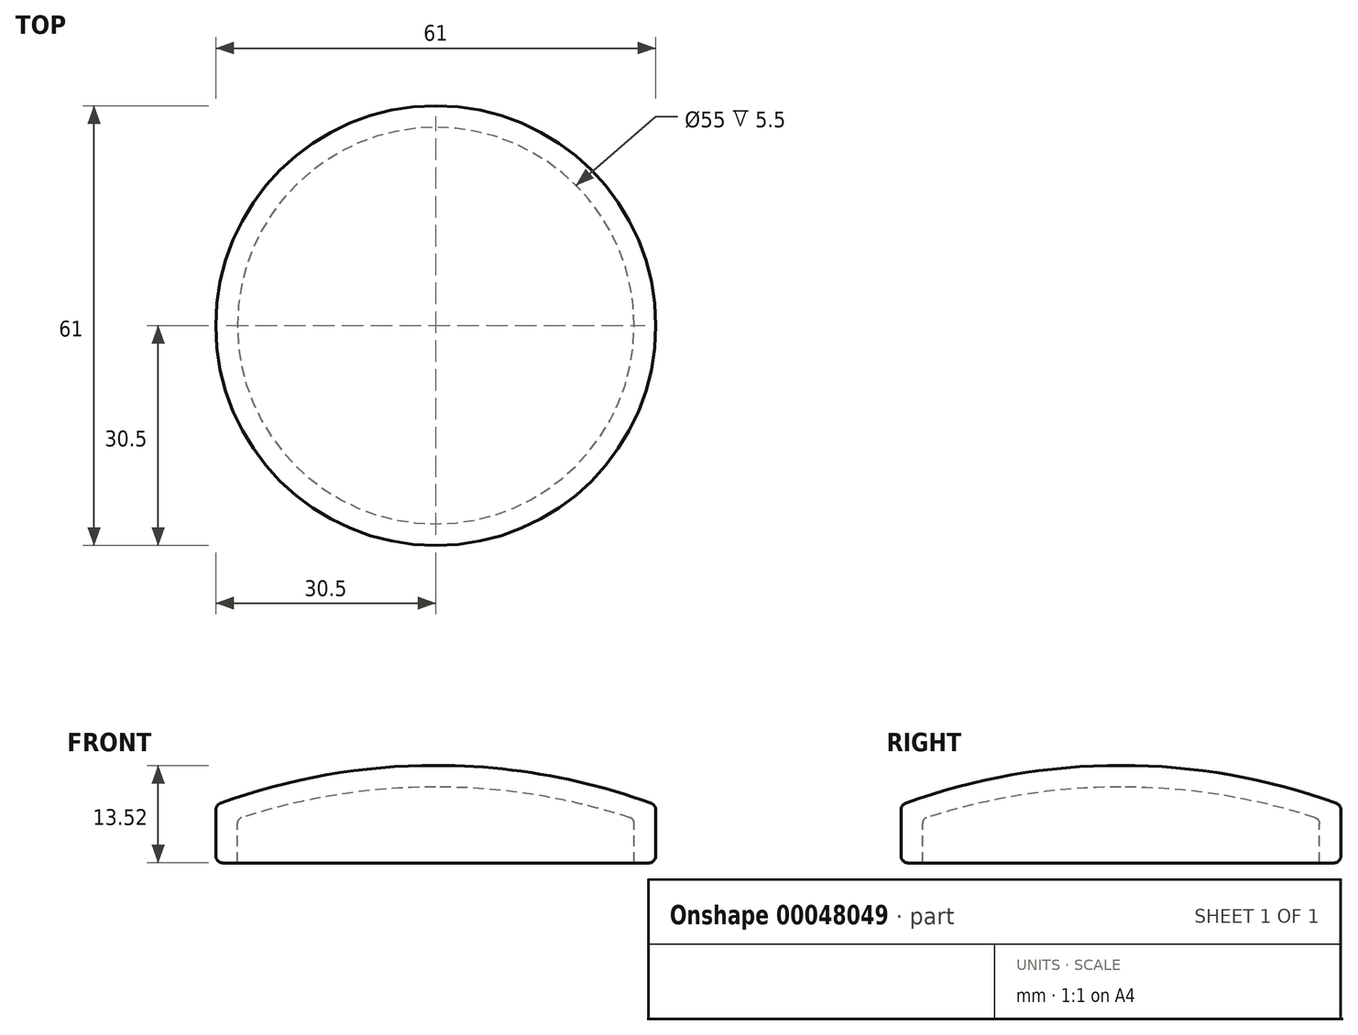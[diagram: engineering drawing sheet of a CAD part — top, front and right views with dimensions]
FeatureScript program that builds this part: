
annotation { "Feature Type Name" : "Feature", "Feature Type Description" : "" }
export const myFeature = defineFeature(function(context is Context, id is Id, definition is map)
    precondition{}
    {
        {
            var Q0;
            Q0=qCreatedBy(makeId("Front.planeOp"),FACE);
            var sketch = newSketch(context, id + "F0", { "sketchPlane" : qUnion([Q0])});
            skLineSegment(sketch, "E0", {"start": v(30.5, 8.28) * mm, "end": v(30.5, 0.26) * mm});
            skLineSegment(sketch, "E1", {"start": v(30.5, 0.26) * mm, "end": v(27.5, 0.26) * mm});
            skLineSegment(sketch, "E2", {"start": v(0, 25.47) * mm, "end": v(0, -11.75) * mm, "construction": true});
            skArc(sketch, "E3", {"start": v(30.5, 8.28) * mm, "mid": v(15.5, 12.4) * mm, "end": v(0, 13.78) * mm});
            skLineSegment(sketch, "E4", {"start": v(0, 13.78) * mm, "end": v(26.52, 13.78) * mm, "construction": true});
            skLineSegment(sketch, "E5", {"start": v(27.5, 1.6) * mm, "end": v(27.5, 1.61) * mm});
            skLineSegment(sketch, "E6", {"start": v(27.5, 0.69) * mm, "end": v(27.5, 1.6) * mm, "construction": true});
            skArc(sketch, "E7", {"start": v(26.95, 6.52) * mm, "mid": v(13.64, 9.7) * mm, "end": v(0, 10.78) * mm});
            skPoint(sketch, "E8.end.orphan", {"position": v(0, 8.36) * mm});
            skLineSegment(sketch, "E9", {"start": v(27.5, 1.61) * mm, "end": v(27.5, 5.76) * mm});
            skPoint(sketch, "E10.visualSharp", {"position": v(27.5, 6.34) * mm});
            skArc(sketch, "E10.filletArc", {"start": v(27.5, 5.76) * mm, "mid": v(27.35, 6.23) * mm, "end": v(26.95, 6.52) * mm});
            skLineSegment(sketch, "E11", {"start": v(26.95, 6.52) * mm, "end": v(26.95, 9.52) * mm, "construction": true});
            skLineSegment(sketch, "E12", {"start": v(0, 13.78) * mm, "end": v(0, 10.78) * mm});
            skLineSegment(sketch, "E13", {"start": v(27.5, 0.26) * mm, "end": v(27.5, 1.6) * mm});
            skSolve(sketch);
        }
        {
            var Q0;
            Q0=makeQuery(id+"F0.imprint","IMPRINT",FACE,{"disambiguationData":[TD([[makeQuery(id+"F0.imprint","IMPRINT",EDGE,{"derivedFrom":sQuery(id+"F0.wireOp",EDGE,"E0")}),-1.0]])]});
            var Q1;
            Q1=sQuery(id+"F0.wireOp",EDGE,"E2");
            revolve(context, id + "F1", {"entities" : qUnion([Q0]), "axis" : qUnion([Q1]), "revolveType" : RevolveType.FULL});
        }
        {
            var Q0;
            Q0=makeQuery(id+"F1.opRevolve","SWEPT_EDGE",EDGE,{"disambiguationData":[OSD([sQuery(id+"F0.wireOp",EDGE,"E0"),sQuery(id+"F0.wireOp",EDGE,"E3")])]});
            var Q1;
            Q1=makeQuery(id+"F1.opRevolve","SWEPT_EDGE",EDGE,{"disambiguationData":[OSD([sQuery(id+"F0.wireOp",EDGE,"E0"),sQuery(id+"F0.wireOp",EDGE,"E1")])]});
            fillet(context, id + "F2", {"entities" : qUnion([Q0, Q1]), "radius" : 1 * mm, "tangentPropagation" : true, "allowEdgeOverflow" : false});
        }
    });
